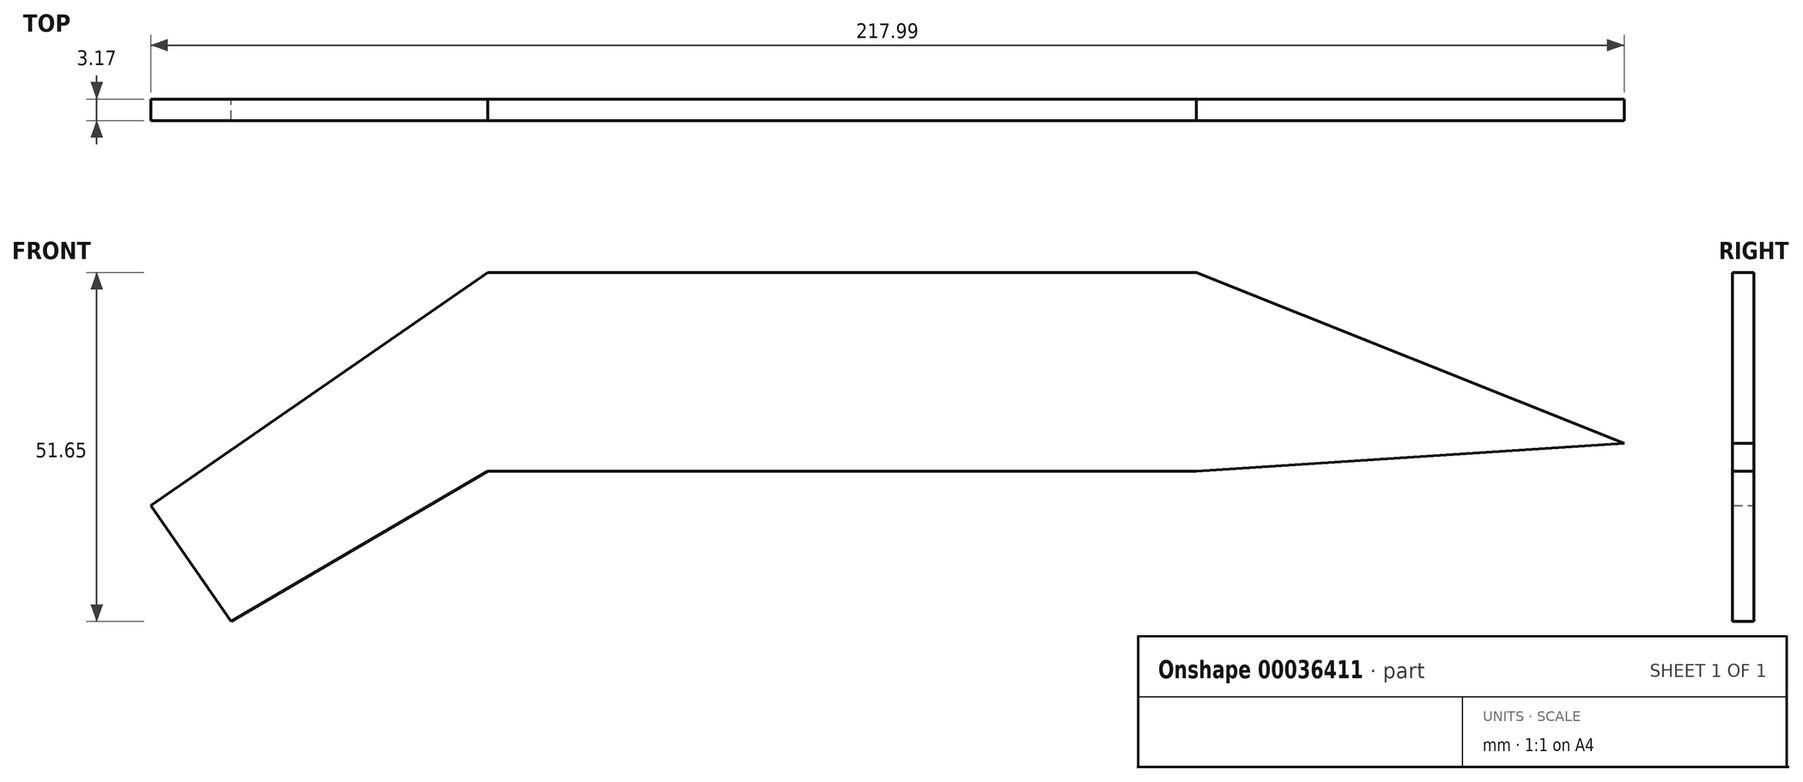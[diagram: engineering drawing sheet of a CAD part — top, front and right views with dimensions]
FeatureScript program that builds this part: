
annotation { "Feature Type Name" : "Feature", "Feature Type Description" : "" }
export const myFeature = defineFeature(function(context is Context, id is Id, definition is map)
    precondition{}
    {
        {
            var Q0;
            Q0=qCreatedBy(makeId("Front.planeOp"),FACE);
            var sketch = newSketch(context, id + "F0", { "sketchPlane" : qUnion([Q0])});
            skLineSegment(sketch, "E0.bottom", {"start": v(0, 0) * mm, "end": v(104.85, 0) * mm});
            skLineSegment(sketch, "E0.top", {"start": v(0, -29.38) * mm, "end": v(104.85, -29.38) * mm});
            skLineSegment(sketch, "E0.left", {"start": v(0, 0) * mm, "end": v(0, -29.38) * mm});
            skLineSegment(sketch, "E0.right", {"start": v(104.85, 0) * mm, "end": v(104.85, -29.38) * mm});
            skLineSegment(sketch, "E1", {"start": v(104.85, 0) * mm, "end": v(168.13, -25.25) * mm});
            skLineSegment(sketch, "E2", {"start": v(168.13, -25.25) * mm, "end": v(104.85, -29.38) * mm});
            skLineSegment(sketch, "E3", {"start": v(0, 0) * mm, "end": v(-49.86, -34.45) * mm});
            skLineSegment(sketch, "E4", {"start": v(-49.86, -34.45) * mm, "end": v(-37.98, -51.65) * mm});
            skLineSegment(sketch, "E5", {"start": v(-37.98, -51.65) * mm, "end": v(0, -29.38) * mm});
            skSolve(sketch);
        }
        {
            var Q0;
            Q0=makeQuery(id+"F0.imprint","IMPRINT",FACE,{"disambiguationData":[TD([[makeQuery(id+"F0.imprint","IMPRINT",EDGE,{"derivedFrom":sQuery(id+"F0.wireOp",EDGE,"E0.bottom")}),-1.0]])]});
            var Q1;
            Q1=makeQuery(id+"F0.imprint","IMPRINT",FACE,{"disambiguationData":[TD([[makeQuery(id+"F0.imprint","IMPRINT",EDGE,{"derivedFrom":sQuery(id+"F0.wireOp",EDGE,"E0.left")}),-1.0]])]});
            var Q2;
            Q2=makeQuery(id+"F0.imprint","IMPRINT",FACE,{"disambiguationData":[TD([[makeQuery(id+"F0.imprint","IMPRINT",EDGE,{"derivedFrom":sQuery(id+"F0.wireOp",EDGE,"E0.right")}),1.0]])]});
            extrude(context, id + "F1", {"entities" : qUnion([Q0, Q1, Q2]), "depth" : 3.17 * mm});
        }
    });
